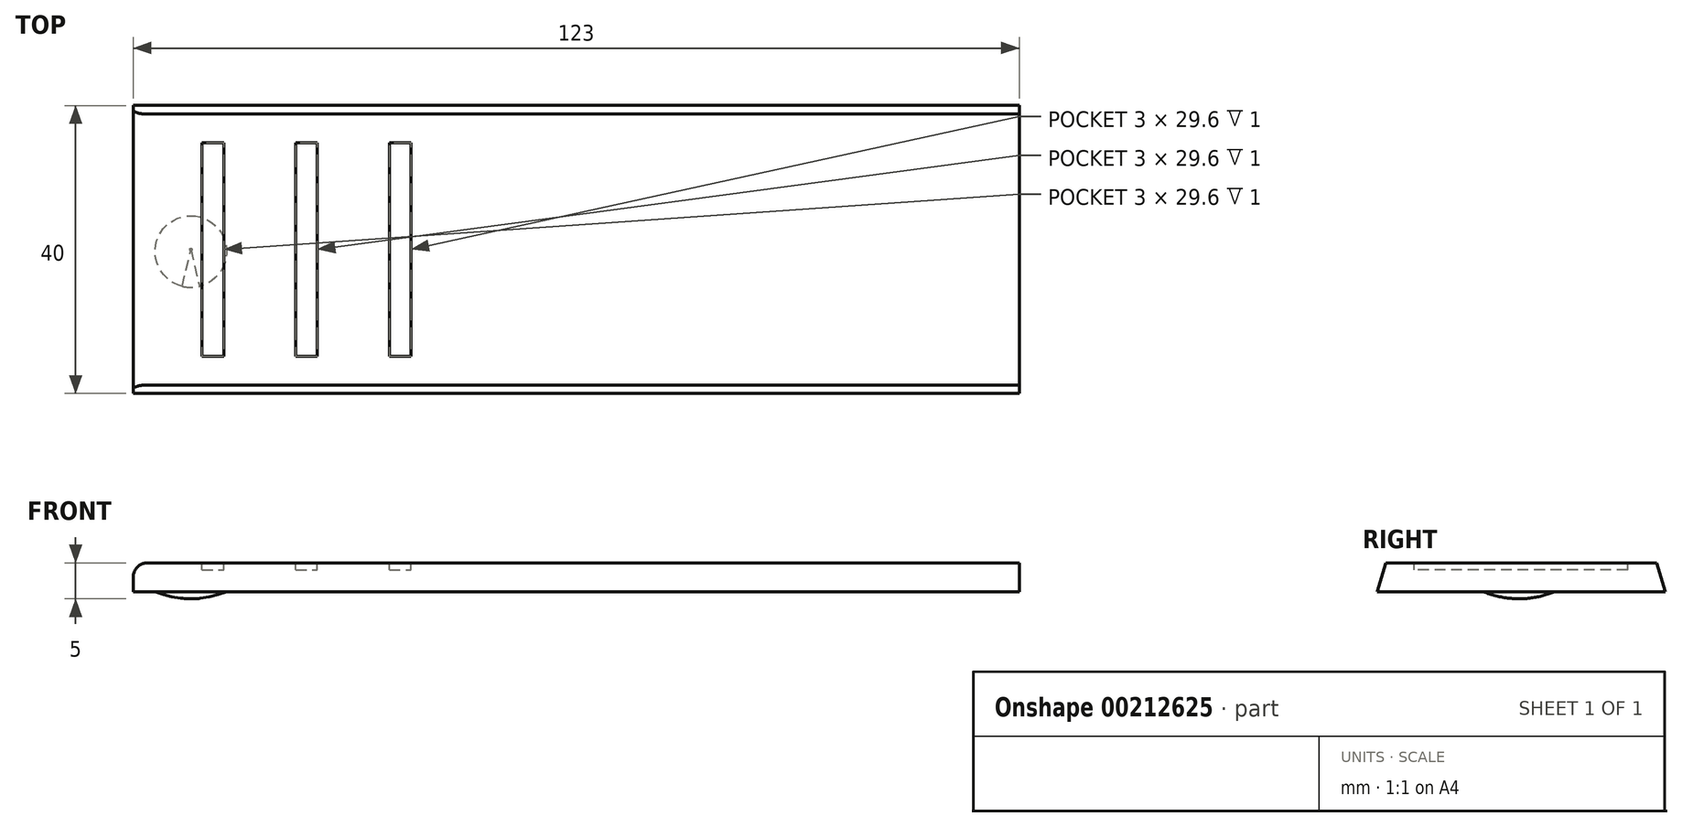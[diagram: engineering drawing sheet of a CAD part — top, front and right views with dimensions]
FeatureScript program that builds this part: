
annotation { "Feature Type Name" : "Feature", "Feature Type Description" : "" }
export const myFeature = defineFeature(function(context is Context, id is Id, definition is map)
    precondition{}
    {
        {
            var Q0;
            Q0=qCreatedBy(makeId("Right.planeOp"),FACE);
            var sketch = newSketch(context, id + "F0", { "sketchPlane" : qUnion([Q0])});
            skLineSegment(sketch, "E0", {"start": v(-15.37, 9.14) * mm, "end": v(22.23, 9.14) * mm});
            skLineSegment(sketch, "E1", {"start": v(22.23, 9.14) * mm, "end": v(23.43, 5.14) * mm});
            skLineSegment(sketch, "E2", {"start": v(23.43, 5.14) * mm, "end": v(-16.57, 5.14) * mm});
            skLineSegment(sketch, "E3", {"start": v(-16.57, 5.14) * mm, "end": v(-15.37, 9.14) * mm});
            skSolve(sketch);
        }
        {
            var Q0;
            Q0=makeQuery(id+"F0.imprint","IMPRINT",FACE,{"disambiguationData":[TD([[makeQuery(id+"F0.imprint","IMPRINT",EDGE,{"derivedFrom":sQuery(id+"F0.wireOp",EDGE,"E0")}),-1.0]])]});
            extrude(context, id + "F1", {"entities" : qUnion([Q0]), "depth" : 123 * mm});
        }
        {
            var Q0;
            Q0=makeQuery(id+"F1.opExtrude","SWEPT_FACE",FACE,{"disambiguationData":[OSD([sQuery(id+"F0.wireOp",EDGE,"E0")])]});
            var sketch = newSketch(context, id + "F2", { "sketchPlane" : qUnion([Q0])});
            skLineSegment(sketch, "E4.bottom", {"start": v(9.56, 18.23) * mm, "end": v(12.56, 18.23) * mm});
            skLineSegment(sketch, "E4.top", {"start": v(9.56, -11.37) * mm, "end": v(12.56, -11.37) * mm});
            skLineSegment(sketch, "E4.left", {"start": v(9.56, 18.23) * mm, "end": v(9.56, -11.37) * mm});
            skLineSegment(sketch, "E4.right", {"start": v(12.56, 18.23) * mm, "end": v(12.56, -11.37) * mm});
            skLineSegment(sketch, "E5.bottom", {"start": v(22.56, 18.23) * mm, "end": v(25.56, 18.23) * mm});
            skLineSegment(sketch, "E5.top", {"start": v(22.56, -11.37) * mm, "end": v(25.56, -11.37) * mm});
            skLineSegment(sketch, "E5.left", {"start": v(22.56, 18.23) * mm, "end": v(22.56, -11.37) * mm});
            skLineSegment(sketch, "E5.right", {"start": v(25.56, 18.23) * mm, "end": v(25.56, -11.37) * mm});
            skLineSegment(sketch, "E6.bottom", {"start": v(35.56, 18.23) * mm, "end": v(38.56, 18.23) * mm});
            skLineSegment(sketch, "E6.top", {"start": v(35.56, -11.37) * mm, "end": v(38.56, -11.37) * mm});
            skLineSegment(sketch, "E6.left", {"start": v(35.56, 18.23) * mm, "end": v(35.56, -11.37) * mm});
            skLineSegment(sketch, "E6.right", {"start": v(38.56, 18.23) * mm, "end": v(38.56, -11.37) * mm});
            skSolve(sketch);
        }
        {
            var Q0;
            Q0=makeQuery(id+"F2.imprint","IMPRINT",FACE,{"disambiguationData":[TD([[makeQuery(id+"F2.imprint","IMPRINT",EDGE,{"derivedFrom":sQuery(id+"F2.wireOp",EDGE,"E4.bottom")}),-1.0]])]});
            var Q1;
            Q1=makeQuery(id+"F2.imprint","IMPRINT",FACE,{"disambiguationData":[TD([[makeQuery(id+"F2.imprint","IMPRINT",EDGE,{"derivedFrom":sQuery(id+"F2.wireOp",EDGE,"E5.bottom")}),-1.0]])]});
            var Q2;
            Q2=makeQuery(id+"F2.imprint","IMPRINT",FACE,{"disambiguationData":[TD([[makeQuery(id+"F2.imprint","IMPRINT",EDGE,{"derivedFrom":sQuery(id+"F2.wireOp",EDGE,"E6.bottom")}),-1.0]])]});
            extrude(context, id + "F3", {"entities" : qUnion([Q0, Q1, Q2]), "operationType" : NewBodyOperationType.REMOVE, "oppositeDirection" : true, "depth" : 1 * mm});
        }
        {
            var Q0;
            Q0=makeQuery(id+"F1.opExtrude","SWEPT_FACE",FACE,{"disambiguationData":[OSD([sQuery(id+"F0.wireOp",EDGE,"E2")])]});
            var sketch = newSketch(context, id + "F4", { "sketchPlane" : qUnion([Q0])});
            skCircle(sketch, "E7", {"center": v(8, -3.43) * mm, "radius": 5.25 * mm});
            skSolve(sketch);
        }
        {
            var Q0;
            Q0=qCreatedBy(makeId("Right.planeOp"),FACE);
            cPlane(context, id + "F5", {"entities" : qUnion([Q0]), "cplaneType" : CPlaneType.OFFSET, "offset" : 8 * mm, "width" : 150 * mm, "height" : 150 * mm});
        }
        {
            var Q0;
            Q0=qCreatedBy(id+"F5.planeOp",FACE);
            var sketch = newSketch(context, id + "F6", { "sketchPlane" : qUnion([Q0])});
            skLineSegment(sketch, "E8", {"start": v(3.43, 5.14) * mm, "end": v(-1.82, 5.14) * mm});
            skLineSegment(sketch, "E9", {"start": v(3.43, 5.14) * mm, "end": v(3.46, 4.14) * mm});
            skArc(sketch, "E10", {"start": v(-1.82, 5.14) * mm, "mid": v(0.77, 4.37) * mm, "end": v(3.46, 4.14) * mm});
            skPoint(sketch, "E11.center.orphan", {"position": v(3.43, 5.14) * mm});
            skSolve(sketch);
        }
        {
            var Q0;
            Q0=makeQuery(id+"F6.imprint","IMPRINT",FACE,{"disambiguationData":[TD([[makeQuery(id+"F6.imprint","IMPRINT",EDGE,{"derivedFrom":sQuery(id+"F6.wireOp",EDGE,"E8")}),1.0]])]});
            var Q1;
            Q1=sQuery(id+"F6.wireOp",EDGE,"E9");
            revolve(context, id + "F7", {"operationType" : NewBodyOperationType.ADD, "entities" : qUnion([Q0]), "axis" : qUnion([Q1]), "revolveType" : RevolveType.FULL});
        }
        {
            var Q0;
            Q0=makeQuery(id+"F1.opExtrude","CAP_EDGE",EDGE,{"disambiguationData":[OSD([sQuery(id+"F0.wireOp",EDGE,"E0")])],"isStart":true});
            fillet(context, id + "F8", {"entities" : qUnion([Q0]), "radius" : 2 * mm, "tangentPropagation" : true, "allowEdgeOverflow" : false});
        }
    });
